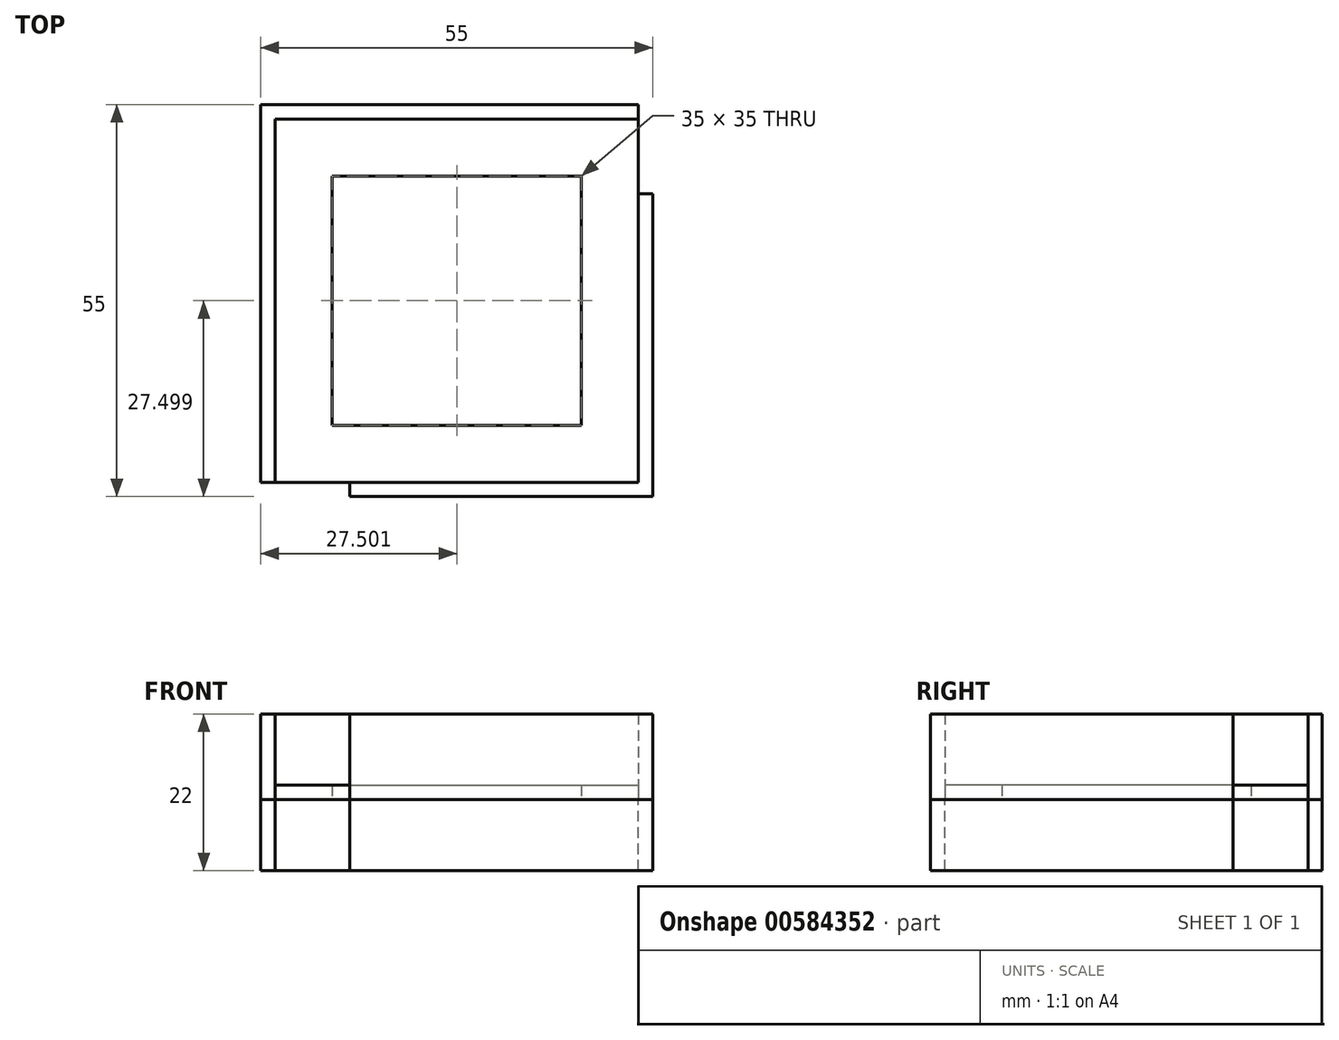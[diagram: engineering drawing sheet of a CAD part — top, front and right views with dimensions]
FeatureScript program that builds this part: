
annotation { "Feature Type Name" : "Feature", "Feature Type Description" : "" }
export const myFeature = defineFeature(function(context is Context, id is Id, definition is map)
    precondition{}
    {
        {
            var Q0;
            Q0=qCreatedBy(makeId("Top.planeOp"),FACE);
            var sketch = newSketch(context, id + "F0", { "sketchPlane" : qUnion([Q0])});
            skLineSegment(sketch, "E0.bottom", {"start": v(-28.72, 28.72) * mm, "end": v(26.28, 28.72) * mm});
            skLineSegment(sketch, "E0.top", {"start": v(-28.72, -26.28) * mm, "end": v(26.28, -26.28) * mm});
            skLineSegment(sketch, "E0.left", {"start": v(-28.72, 28.72) * mm, "end": v(-28.72, -26.28) * mm});
            skLineSegment(sketch, "E0.right", {"start": v(26.28, 28.72) * mm, "end": v(26.28, -26.28) * mm});
            skPoint(sketch, "E0.middle", {"position": v(-1.22, 1.22) * mm});
            skLineSegment(sketch, "E1.0", {"start": v(-26.72, 26.72) * mm, "end": v(24.28, 26.72) * mm});
            skLineSegment(sketch, "E1.1", {"start": v(-26.72, 26.72) * mm, "end": v(-26.72, -24.28) * mm});
            skLineSegment(sketch, "E1.2", {"start": v(-26.72, -24.28) * mm, "end": v(24.28, -24.28) * mm});
            skLineSegment(sketch, "E1.3", {"start": v(24.28, 26.72) * mm, "end": v(24.28, -24.28) * mm});
            skLineSegment(sketch, "E2", {"start": v(-18.72, -24.28) * mm, "end": v(-18.72, -26.28) * mm});
            skLineSegment(sketch, "E3", {"start": v(-16.22, -24.28) * mm, "end": v(-16.22, -26.28) * mm});
            skLineSegment(sketch, "E4", {"start": v(24.28, 18.72) * mm, "end": v(26.28, 18.72) * mm});
            skLineSegment(sketch, "E5", {"start": v(24.28, 16.22) * mm, "end": v(26.28, 16.22) * mm});
            skCircle(sketch, "E6", {"center": v(-1.22, 1.22) * mm, "radius": 5 * mm});
            skLineSegment(sketch, "E7", {"start": v(24.28, 26.72) * mm, "end": v(24.28, 28.72) * mm});
            skLineSegment(sketch, "E8", {"start": v(-26.72, -24.28) * mm, "end": v(-28.72, -24.28) * mm});
            skLineSegment(sketch, "E9.0", {"start": v(-18.72, 18.72) * mm, "end": v(-18.72, -16.28) * mm});
            skLineSegment(sketch, "E9.1", {"start": v(-18.72, 18.72) * mm, "end": v(16.28, 18.72) * mm});
            skLineSegment(sketch, "E9.2", {"start": v(16.28, 18.72) * mm, "end": v(16.28, -16.28) * mm});
            skLineSegment(sketch, "E9.3", {"start": v(-18.72, -16.28) * mm, "end": v(16.28, -16.28) * mm});
            skSolve(sketch);
        }
        {
            var Q0;
            Q0=makeQuery(id+"F0.imprint","IMPRINT",FACE,{"disambiguationData":[TD([[makeQuery(id+"F0.imprint","IMPRINT",EDGE,{"derivedFrom":sQuery(id+"F0.wireOp",EDGE,"E1.0")}),1.0]])]});
            var Q1;
            {var subQ4=sQuery(id+"F0.wireOp",EDGE,"E3");Q1=makeQuery(id+"F0.imprint","IMPRINT",FACE,{"disambiguationData":[TD([[makeQuery(id+"F0.imprint","IMPRINT",EDGE,{"derivedFrom":subQ4}),1.0]])]});}
            extrude(context, id + "F1", {"entities" : qUnion([Q0, Q1]), "depth" : 12 * mm, "offsetDistance" : 25 * mm});
        }
        {
            var Q0;
            {var subQ4=sQuery(id+"F0.wireOp",EDGE,"E1.0");Q0=makeQuery(id+"F0.imprint","IMPRINT",FACE,{"disambiguationData":[TD([[makeQuery(id+"F0.imprint","IMPRINT",EDGE,{"derivedFrom":subQ4}),-1.0]])]});}
            var Q1;
            Q1=makeQuery(id+"F0.imprint","IMPRINT",FACE,{"disambiguationData":[TD([[makeQuery(id+"F0.imprint","IMPRINT",EDGE,{"derivedFrom":sQuery(id+"F0.wireOp",EDGE,"E6")}),1.0]])]});
            extrude(context, id + "F2", {"entities" : qUnion([Q0, Q1]), "depth" : 2 * mm, "offsetDistance" : 25 * mm});
        }
        {
            var Q0;
            Q0=makeQuery(id+"F0.imprint","IMPRINT",FACE,{"disambiguationData":[TD([[makeQuery(id+"F0.imprint","IMPRINT",EDGE,{"derivedFrom":sQuery(id+"F0.wireOp",EDGE,"E1.0")}),1.0]])]});
            var Q1;
            {var subQ4=sQuery(id+"F0.wireOp",EDGE,"E3");Q1=makeQuery(id+"F0.imprint","IMPRINT",FACE,{"disambiguationData":[TD([[makeQuery(id+"F0.imprint","IMPRINT",EDGE,{"derivedFrom":subQ4}),1.0]])]});}
            extrude(context, id + "F3", {"entities" : qUnion([Q0, Q1]), "oppositeDirection" : true, "depth" : 10 * mm, "offsetDistance" : 25 * mm});
        }
        {
            var Q0;
            Q0=makeQuery(id+"F2.opExtrude","SWEPT_BODY",BODY,{"disambiguationData":[OSD([sQuery(id+"F0.wireOp",EDGE,"E6")])]});
            deleteBodies(context, id + "F4", {"entities" : qUnion([Q0])});
        }
    });
